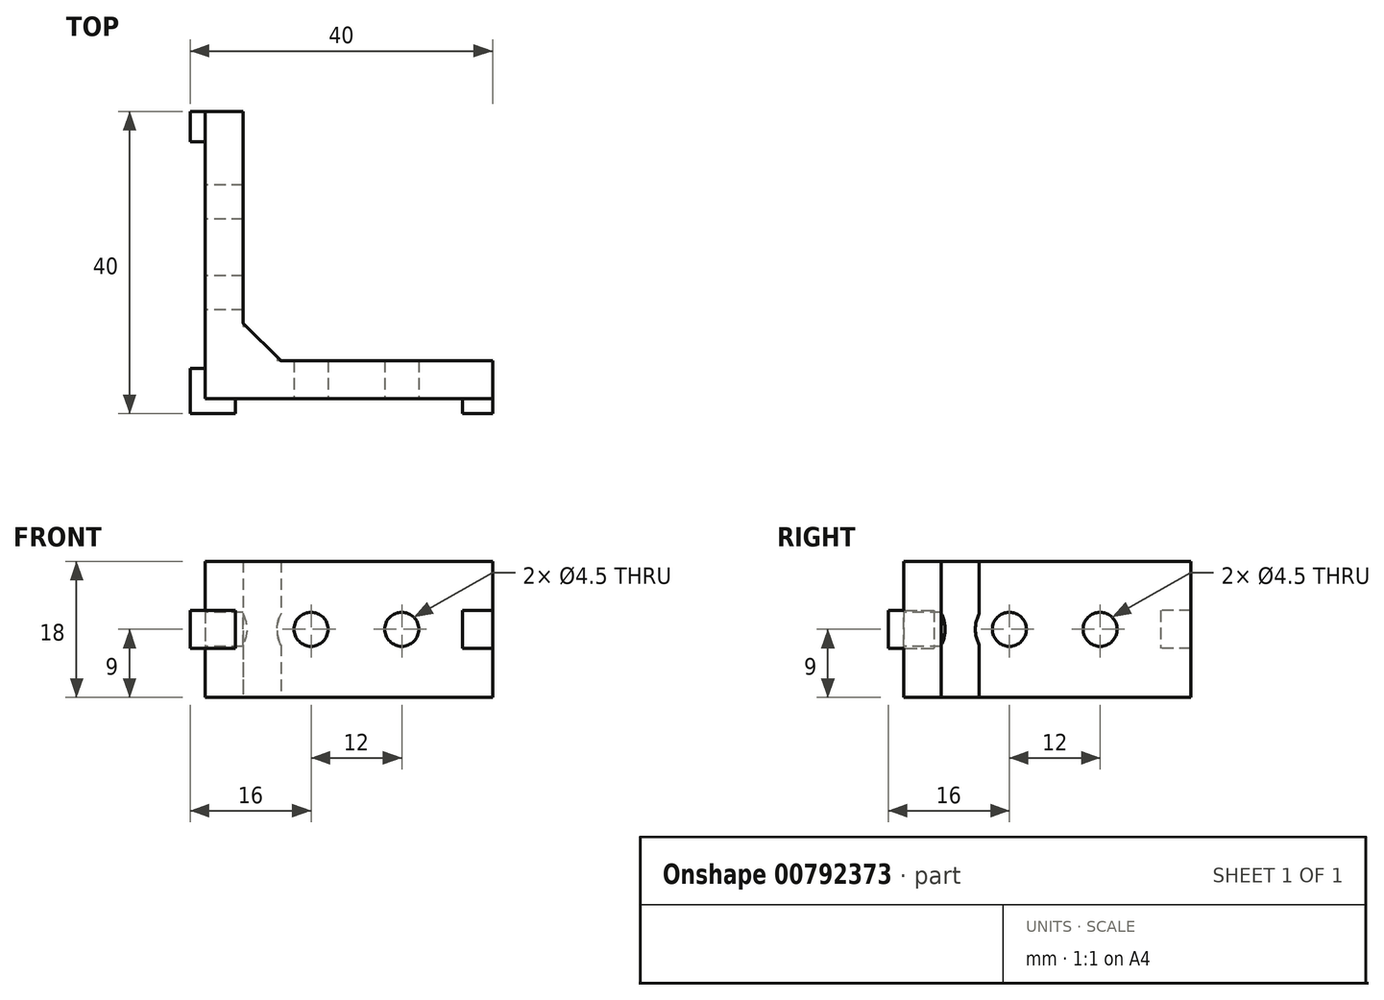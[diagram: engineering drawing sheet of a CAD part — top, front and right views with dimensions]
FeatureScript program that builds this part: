
annotation { "Feature Type Name" : "Feature", "Feature Type Description" : "" }
export const myFeature = defineFeature(function(context is Context, id is Id, definition is map)
    precondition{}
    {
        {
            var Q0;
            Q0=qCreatedBy(makeId("Top.planeOp"),FACE);
            var sketch = newSketch(context, id + "F0", { "sketchPlane" : qUnion([Q0])});
            skLineSegment(sketch, "E0", {"start": v(0, 0) * mm, "end": v(0, 38) * mm});
            skLineSegment(sketch, "E1", {"start": v(0, 0) * mm, "end": v(38, 0) * mm});
            skLineSegment(sketch, "E2", {"start": v(0, 38) * mm, "end": v(5, 38) * mm});
            skLineSegment(sketch, "E3", {"start": v(5, 38) * mm, "end": v(5, 10) * mm});
            skLineSegment(sketch, "E4", {"start": v(10, 5) * mm, "end": v(38, 5) * mm});
            skLineSegment(sketch, "E5", {"start": v(38, 5) * mm, "end": v(38, 0) * mm});
            skLineSegment(sketch, "E6", {"start": v(5, 10) * mm, "end": v(10, 5) * mm});
            skSolve(sketch);
        }
        {
            var Q0;
            Q0=makeQuery(id+"F0.imprint","IMPRINT",FACE,{"disambiguationData":[TD([[makeQuery(id+"F0.imprint","IMPRINT",EDGE,{"derivedFrom":sQuery(id+"F0.wireOp",EDGE,"E0")}),-1.0]])]});
            extrude(context, id + "F1", {"entities" : qUnion([Q0]), "depth" : 18 * mm, "offsetDistance" : 25 * mm});
        }
        {
            var Q0;
            Q0=makeQuery(id+"F1.opExtrude","SWEPT_FACE",FACE,{"disambiguationData":[OSD([sQuery(id+"F0.wireOp",EDGE,"E1")])]});
            var sketch = newSketch(context, id + "F2", { "sketchPlane" : qUnion([Q0])});
            skLineSegment(sketch, "E7", {"start": v(0, 9) * mm, "end": v(38, 9) * mm, "construction": true});
            skCircle(sketch, "E8", {"center": v(26, 9) * mm, "radius": 2.25 * mm});
            skCircle(sketch, "E9", {"center": v(14, 9) * mm, "radius": 2.25 * mm});
            skLineSegment(sketch, "E10.bottom", {"start": v(38, 11.5) * mm, "end": v(34, 11.5) * mm});
            skLineSegment(sketch, "E10.top", {"start": v(38, 6.5) * mm, "end": v(34, 6.5) * mm});
            skLineSegment(sketch, "E10.left", {"start": v(38, 11.5) * mm, "end": v(38, 6.5) * mm});
            skLineSegment(sketch, "E10.right", {"start": v(34, 11.5) * mm, "end": v(34, 6.5) * mm});
            skLineSegment(sketch, "E11.bottom", {"start": v(0, 11.5) * mm, "end": v(4, 11.5) * mm});
            skLineSegment(sketch, "E11.top", {"start": v(0, 6.5) * mm, "end": v(4, 6.5) * mm});
            skLineSegment(sketch, "E11.left", {"start": v(0, 11.5) * mm, "end": v(0, 6.5) * mm});
            skLineSegment(sketch, "E11.right", {"start": v(4, 11.5) * mm, "end": v(4, 6.5) * mm});
            skSolve(sketch);
        }
        {
            var Q0;
            Q0=makeQuery(id+"F2.imprint","IMPRINT",FACE,{"disambiguationData":[TD([[makeQuery(id+"F2.imprint","IMPRINT",EDGE,{"derivedFrom":sQuery(id+"F2.wireOp",EDGE,"E11.bottom")}),-1.0]])]});
            var Q1;
            Q1=makeQuery(id+"F2.imprint","IMPRINT",FACE,{"disambiguationData":[TD([[makeQuery(id+"F2.imprint","IMPRINT",EDGE,{"derivedFrom":sQuery(id+"F2.wireOp",EDGE,"E10.bottom")}),1.0]])]});
            extrude(context, id + "F3", {"entities" : qUnion([Q0, Q1]), "operationType" : NewBodyOperationType.ADD, "depth" : 2 * mm, "offsetDistance" : 25 * mm});
        }
        {
            var Q0;
            Q0=makeQuery(id+"F2.imprint","IMPRINT",FACE,{"disambiguationData":[TD([[makeQuery(id+"F2.imprint","IMPRINT",EDGE,{"derivedFrom":sQuery(id+"F2.wireOp",EDGE,"E9")}),1.0]])]});
            var Q1;
            Q1=makeQuery(id+"F2.imprint","IMPRINT",FACE,{"disambiguationData":[TD([[makeQuery(id+"F2.imprint","IMPRINT",EDGE,{"derivedFrom":sQuery(id+"F2.wireOp",EDGE,"E8")}),1.0]])]});
            extrude(context, id + "F4", {"entities" : qUnion([Q0, Q1]), "operationType" : NewBodyOperationType.REMOVE, "oppositeDirection" : true, "depth" : 25 * mm, "offsetDistance" : 25 * mm});
        }
        {
            var Q0;
            Q0=makeQuery(id+"F1.opExtrude","SWEPT_FACE",FACE,{"disambiguationData":[OSD([sQuery(id+"F0.wireOp",EDGE,"E4")])]});
            var sketch = newSketch(context, id + "F5", { "sketchPlane" : qUnion([Q0])});
            skCircle(sketch, "E12", {"center": v(-14, 9) * mm, "radius": 4.5 * mm});
            skSolve(sketch);
        }
        {
            var Q0;
            Q0 = qSketchRegion(id + "F5", true);
            extrude(context, id + "F6", {"entities" : qUnion([Q0]), "operationType" : NewBodyOperationType.REMOVE, "depth" : 25 * mm, "offsetDistance" : 25 * mm});
        }
        {
            var Q0;
            Q0=makeQuery(id+"F3.boolean.opBoolean","MERGE",FACE,{"derivedFrom":[makeQuery(id+"F1.opExtrude","SWEPT_FACE",FACE,{"disambiguationData":[OSD([sQuery(id+"F0.wireOp",EDGE,"E0")])]}),makeQuery(id+"F3.opExtrude","SWEPT_FACE",FACE,{"disambiguationData":[OSD([sQuery(id+"F2.wireOp",EDGE,"E11.left")])]})]});
            var sketch = newSketch(context, id + "F7", { "sketchPlane" : qUnion([Q0])});
            skLineSegment(sketch, "E13", {"start": v(2, 9) * mm, "end": v(-38, 9) * mm, "construction": true});
            skCircle(sketch, "E14", {"center": v(-14, 9) * mm, "radius": 2.25 * mm});
            skCircle(sketch, "E15", {"center": v(-26, 9) * mm, "radius": 2.25 * mm});
            skLineSegment(sketch, "E16.bottom", {"start": v(2, 11.5) * mm, "end": v(-4, 11.5) * mm});
            skLineSegment(sketch, "E16.top", {"start": v(2, 6.5) * mm, "end": v(-4, 6.5) * mm});
            skLineSegment(sketch, "E16.left", {"start": v(2, 11.5) * mm, "end": v(2, 6.5) * mm});
            skLineSegment(sketch, "E16.right", {"start": v(-4, 11.5) * mm, "end": v(-4, 6.5) * mm});
            skLineSegment(sketch, "E17.bottom", {"start": v(-38, 11.5) * mm, "end": v(-34, 11.5) * mm});
            skLineSegment(sketch, "E17.top", {"start": v(-38, 6.5) * mm, "end": v(-34, 6.5) * mm});
            skLineSegment(sketch, "E17.left", {"start": v(-38, 11.5) * mm, "end": v(-38, 6.5) * mm});
            skLineSegment(sketch, "E17.right", {"start": v(-34, 11.5) * mm, "end": v(-34, 6.5) * mm});
            skSolve(sketch);
        }
        {
            var Q0;
            Q0=makeQuery(id+"F7.imprint","IMPRINT",FACE,{"disambiguationData":[TD([[makeQuery(id+"F7.imprint","IMPRINT",EDGE,{"derivedFrom":sQuery(id+"F7.wireOp",EDGE,"E14")}),1.0]])]});
            var Q1;
            Q1=makeQuery(id+"F7.imprint","IMPRINT",FACE,{"disambiguationData":[TD([[makeQuery(id+"F7.imprint","IMPRINT",EDGE,{"derivedFrom":sQuery(id+"F7.wireOp",EDGE,"E15")}),1.0]])]});
            extrude(context, id + "F8", {"entities" : qUnion([Q0, Q1]), "operationType" : NewBodyOperationType.REMOVE, "oppositeDirection" : true, "depth" : 25 * mm, "offsetDistance" : 25 * mm});
        }
        {
            var Q0;
            {var subQ0=sQuery(id+"F7.wireOp",EDGE,"E16.left");Q0=makeQuery(id+"F7.imprint","IMPRINT",FACE,{"disambiguationData":[TD([[makeQuery(id+"F7.imprint","IMPRINT",EDGE,{"derivedFrom":subQ0}),-1.0]])]});}
            var Q1;
            Q1=makeQuery(id+"F7.imprint","IMPRINT",FACE,{"disambiguationData":[TD([[makeQuery(id+"F7.imprint","IMPRINT",EDGE,{"derivedFrom":sQuery(id+"F7.wireOp",EDGE,"E17.bottom")}),-1.0]])]});
            extrude(context, id + "F9", {"entities" : qUnion([Q0, Q1]), "operationType" : NewBodyOperationType.ADD, "depth" : 2 * mm, "offsetDistance" : 25 * mm});
        }
        {
            var Q0;
            Q0=makeQuery(id+"F1.opExtrude","SWEPT_FACE",FACE,{"disambiguationData":[OSD([sQuery(id+"F0.wireOp",EDGE,"E3")])]});
            var sketch = newSketch(context, id + "F10", { "sketchPlane" : qUnion([Q0])});
            skCircle(sketch, "E18", {"center": v(14, 9) * mm, "radius": 4.5 * mm});
            skSolve(sketch);
        }
        {
            var Q0;
            Q0 = qSketchRegion(id + "F10", true);
            extrude(context, id + "F11", {"entities" : qUnion([Q0]), "operationType" : NewBodyOperationType.REMOVE, "depth" : 25 * mm, "offsetDistance" : 25 * mm});
        }
    });
